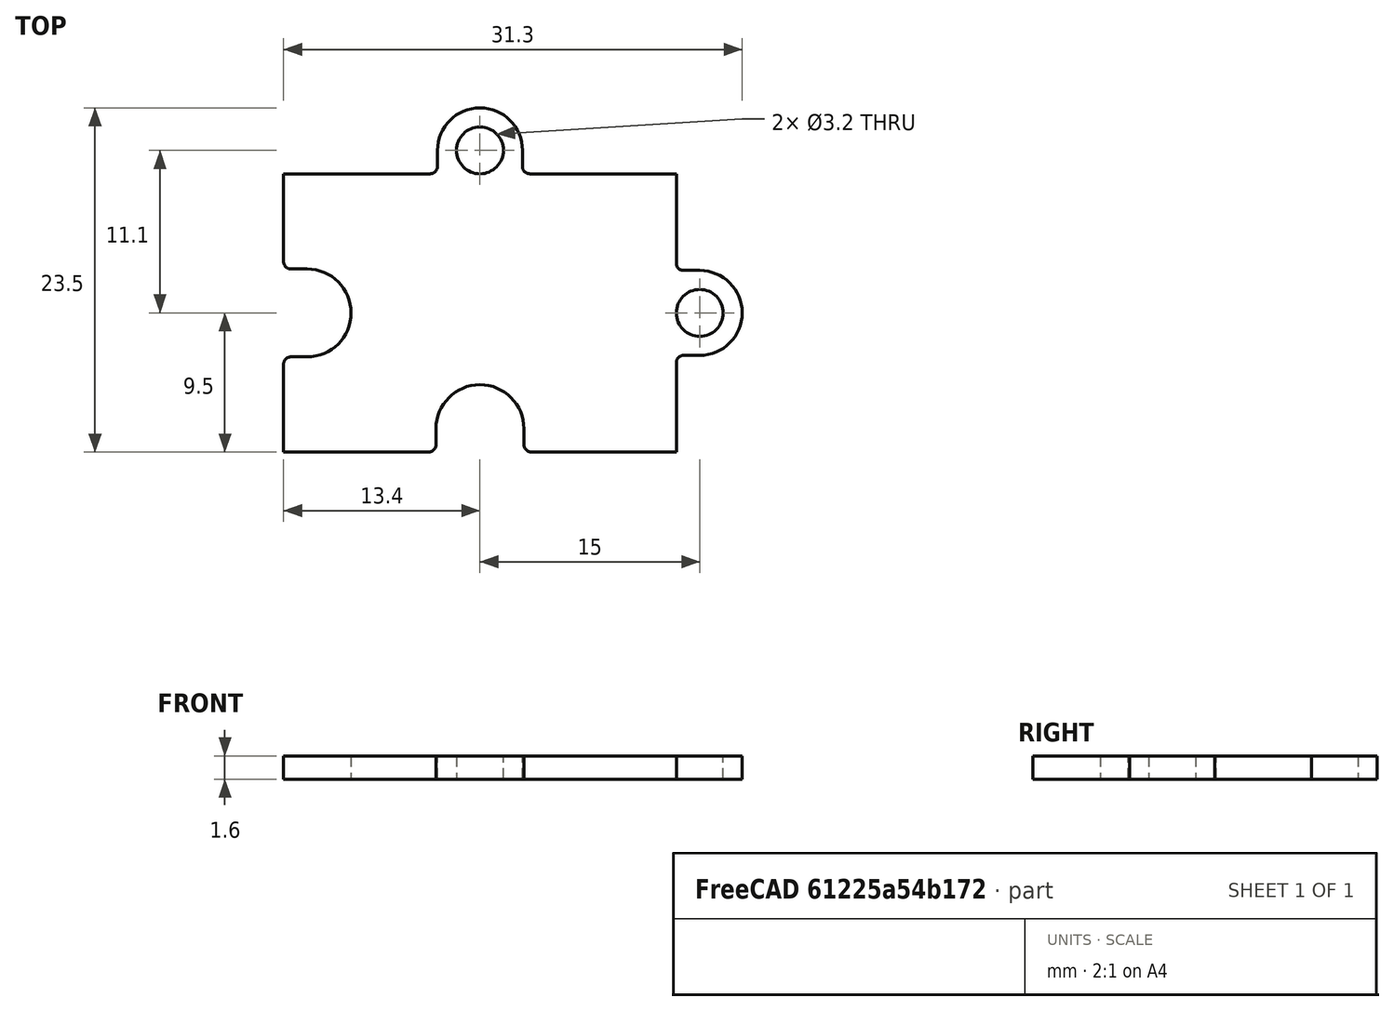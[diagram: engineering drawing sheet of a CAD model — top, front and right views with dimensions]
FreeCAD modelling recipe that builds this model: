
FCSTD DOCUMENT  (FreeCAD 0.14R3702 (Git))
Label: PCB_octopus
License: CC-BY 3.0
LicenseURL: http://creativecommons.org/licenses/by/3.0/
objects: Sketcher::SketchObject×1, PartDesign::Pad×1, Part::Feature×1
note: 4 computed .brp shape members not serialized (recipe doc carries the construction recipe); baked Part::Feature solids carry a one-line shape summary decoded from their .brp

FEATURE [Sketcher::SketchObject] Sketch004  label="octopus-pcb-base-sketch"
  sketch-geometry (36):
    g0: LineSegment StartX=-13.4 StartY=9.5 StartZ=0 EndX=-3.4 EndY=9.5 EndZ=0
    g1: LineSegment StartX=13.4 StartY=9.5 StartZ=0 EndX=13.4 EndY=3.4 EndZ=0
    g2: LineSegment StartX=13.4 StartY=-9.5 StartZ=0 EndX=3.5 EndY=-9.5 EndZ=0
    g3: LineSegment StartX=-13.4 StartY=-9.5 StartZ=0 EndX=-13.4 EndY=-3.5 EndZ=0
    g4: Circle CenterX=0 CenterY=11.1 CenterZ=0 NormalX=0 NormalY=0 NormalZ=1 Radius=1.6
    g5: LineSegment StartX=3.4 StartY=9.5 StartZ=0 EndX=13.4 EndY=9.5 EndZ=0
    g6: Circle CenterX=15 CenterY=0 CenterZ=0 NormalX=0 NormalY=0 NormalZ=1 Radius=1.6
    g7: LineSegment StartX=13.4 StartY=-3.4 StartZ=0 EndX=13.4 EndY=-9.5 EndZ=0
    g8: LineSegment StartX=-3.5 StartY=-9.5 StartZ=0 EndX=-13.4 EndY=-9.5 EndZ=0
    g9: LineSegment StartX=-13.4 StartY=3.5 StartZ=0 EndX=-13.4 EndY=9.5 EndZ=0
    g10: LineSegment [constr] StartX=-2.9 StartY=11.1 StartZ=0 EndX=2.9 EndY=11.1 EndZ=0
    g11: ArcOfCircle CenterX=0 CenterY=11.1 CenterZ=0 NormalX=0 NormalY=0 NormalZ=1 Radius=2.9 StartAngle=0 EndAngle=3.14159
    g12: LineSegment StartX=2.9 StartY=11.1 StartZ=0 EndX=2.9 EndY=10 EndZ=0
    g13: LineSegment StartX=-2.9 StartY=11.1 StartZ=0 EndX=-2.9 EndY=10 EndZ=0
    g14: LineSegment [constr] StartX=15 StartY=2.9 StartZ=0 EndX=15 EndY=-2.9 EndZ=0
    g15: LineSegment StartX=13.9 StartY=2.9 StartZ=0 EndX=15 EndY=2.9 EndZ=0
    g16: LineSegment StartX=13.9 StartY=-2.9 StartZ=0 EndX=15 EndY=-2.9 EndZ=0
    g17: ArcOfCircle CenterX=15 CenterY=0 CenterZ=0 NormalX=0 NormalY=0 NormalZ=1 Radius=2.9 StartAngle=4.71239 EndAngle=7.85398
    g18: LineSegment [constr] StartX=-3 StartY=-7.9 StartZ=0 EndX=3 EndY=-7.9 EndZ=0
    g19: ArcOfCircle CenterX=0 CenterY=-7.9 CenterZ=0 NormalX=0 NormalY=0 NormalZ=1 Radius=3 StartAngle=0 EndAngle=3.14159
    g20: Circle [constr] CenterX=0 CenterY=-7.9 CenterZ=0 NormalX=0 NormalY=0 NormalZ=1 Radius=1.6
    g21: LineSegment StartX=-3 StartY=-7.9 StartZ=0 EndX=-3 EndY=-9 EndZ=0
    g22: LineSegment StartX=3 StartY=-7.9 StartZ=0 EndX=3 EndY=-9 EndZ=0
    g23: ArcOfCircle CenterX=-11.8 CenterY=0 CenterZ=0 NormalX=0 NormalY=0 NormalZ=1 Radius=3 StartAngle=4.71239 EndAngle=7.85398
    g24: LineSegment [constr] StartX=-11.8 StartY=3 StartZ=0 EndX=-11.8 EndY=-3 EndZ=0
    g25: LineSegment StartX=-12.9 StartY=3 StartZ=0 EndX=-11.8 EndY=3 EndZ=0
    g26: LineSegment StartX=-12.9 StartY=-3 StartZ=0 EndX=-11.8 EndY=-3 EndZ=0
    g27: Circle [constr] CenterX=-11.8 CenterY=0 CenterZ=0 NormalX=0 NormalY=0 NormalZ=1 Radius=1.6
    g28: ArcOfCircle CenterX=3.4 CenterY=10 CenterZ=0 NormalX=0 NormalY=0 NormalZ=1 Radius=0.5 StartAngle=3.14159 EndAngle=4.71239
    g29: ArcOfCircle CenterX=-3.4 CenterY=10 CenterZ=0 NormalX=0 NormalY=0 NormalZ=1 Radius=0.5 StartAngle=4.71239 EndAngle=6.28319
    g30: ArcOfCircle CenterX=13.9 CenterY=3.4 CenterZ=0 NormalX=0 NormalY=0 NormalZ=1 Radius=0.5 StartAngle=3.14159 EndAngle=4.71239
    g31: ArcOfCircle CenterX=13.9 CenterY=-3.4 CenterZ=0 NormalX=0 NormalY=0 NormalZ=1 Radius=0.5 StartAngle=1.5708 EndAngle=3.14159
    g32: ArcOfCircle CenterX=3.5 CenterY=-9 CenterZ=0 NormalX=0 NormalY=0 NormalZ=1 Radius=0.5 StartAngle=3.14159 EndAngle=4.71239
    g33: ArcOfCircle CenterX=-3.5 CenterY=-9 CenterZ=0 NormalX=0 NormalY=0 NormalZ=1 Radius=0.5 StartAngle=4.71239 EndAngle=6.28319
    g34: ArcOfCircle CenterX=-12.9 CenterY=-3.5 CenterZ=0 NormalX=0 NormalY=0 NormalZ=1 Radius=0.5 StartAngle=1.5708 EndAngle=3.14159
    g35: ArcOfCircle CenterX=-12.9 CenterY=3.5 CenterZ=0 NormalX=0 NormalY=0 NormalZ=1 Radius=0.5 StartAngle=3.14159 EndAngle=4.71239
  constraints (94):
    c: Coincident(g5,g1)
    c: Coincident(g7,g2)
    c: Coincident(g8,g3)
    c: Coincident(g9,g0)
    c: Horizontal(g0)
    c: Horizontal(g2)
    c: Vertical(g1)
    c: Vertical(g3)
    c: Radius(g4) = 1.6
    c: Tangent(g0,g5)
    c: Equal(g6,g4)
    c: Tangent(g1,g7)
    c: PointOnObject(g6,g-1)
    c: Tangent(g2,g8)
    c: Tangent(g3,g9)
    c: PointOnObject(g4,g-2)
    c: Symmetric(g1,g2,g-1)
    c: Symmetric(g1,g0,g-2)
    c: Tangent(g5,g4)
    c: Symmetric(g10,g10,g-2)
    c: PointOnObject(g4,g10)
    c: Coincident(g11,g10)
    c: Coincident(g10,g11)
    c: Coincident(g11,g4)
    c: Vertical(g12)
    c: Coincident(g12,g10)
    c: Vertical(g13)
    c: Coincident(g13,g10)
    c: DistanceX(g10,g10) = 5.8
    c: Vertical(g14)
    c: PointOnObject(g6,g14)
    c: Symmetric(g14,g14,g-1)
    c: Tangent(g6,g1)
    c: Horizontal(g15)
    c: Coincident(g15,g14)
    c: Horizontal(g16)
    c: Coincident(g16,g14)
    c: Equal(g10,g14)
    c: Coincident(g17,g6)
    c: Coincident(g17,g14)
    c: Coincident(g17,g14)
    c: Horizontal(g18)
    c: Symmetric(g18,g18,g-2)
    c: DistanceX(g18) = 6
    c: Coincident(g19,g18)
    c: Coincident(g19,g18)
    c: PointOnObject(g19,g18)
    c: PointOnObject(g20,g-2)
    c: Tangent(g20,g2)
    c: Coincident(g19,g20)
    c: Equal(g20,g4)
    c: Vertical(g22)
    c: Vertical(g21)
    c: Coincident(g21,g18)
    c: Coincident(g22,g18)
    c: PointOnObject(g23,g-1)
    c: Symmetric(g24,g24,g-1)
    c: Coincident(g24,g23)
    c: Coincident(g23,g24)
    c: Equal(g24,g18)
    c: PointOnObject(g23,g24)
    c: Horizontal(g25)
    c: Horizontal(g26)
    c: Coincident(g27,g23)
    c: Equal(g27,g20)
    c: Tangent(g27,g9)
    c: Coincident(g25,g23)
    c: Coincident(g26,g23)
    c: DistanceY(g1,g2) = -19
    c: DistanceX(g0,g1) = 26.8
    c: Tangent(g5,g28)
    c: Tangent(g12,g28)
    c: Radius(g28) = 0.5
    c: Tangent(g0,g29)
    c: Tangent(g13,g29)
    c: Equal(g29,g28)
    c: Tangent(g1,g30)
    c: Tangent(g15,g30)
    c: Tangent(g7,g31)
    c: Tangent(g16,g31)
    c: Equal(g28,g30)
    c: Equal(g30,g31)
    c: Tangent(g2,g32)
    c: Tangent(g22,g32)
    c: Tangent(g8,g33)
    c: Tangent(g21,g33)
    c: Equal(g31,g32)
    c: Equal(g32,g33)
    c: Tangent(g3,g34)
    c: Tangent(g26,g34)
    c: Tangent(g9,g35)
    c: Tangent(g25,g35)
    c: Equal(g35,g34)
    c: Equal(g34,g33)
FEATURE [PartDesign::Pad] Pad003  label="octopus-pcb-base"
  Length = 1.6
  Length2 = 100
  Sketch = -> Sketch004
  Type = 0
FEATURE [Part::Feature] Pad003001  label="octopus-pcb-final"
  shape: bbox 31.3 x 23.5 x 1.6 mm, 32 faces (baked)
